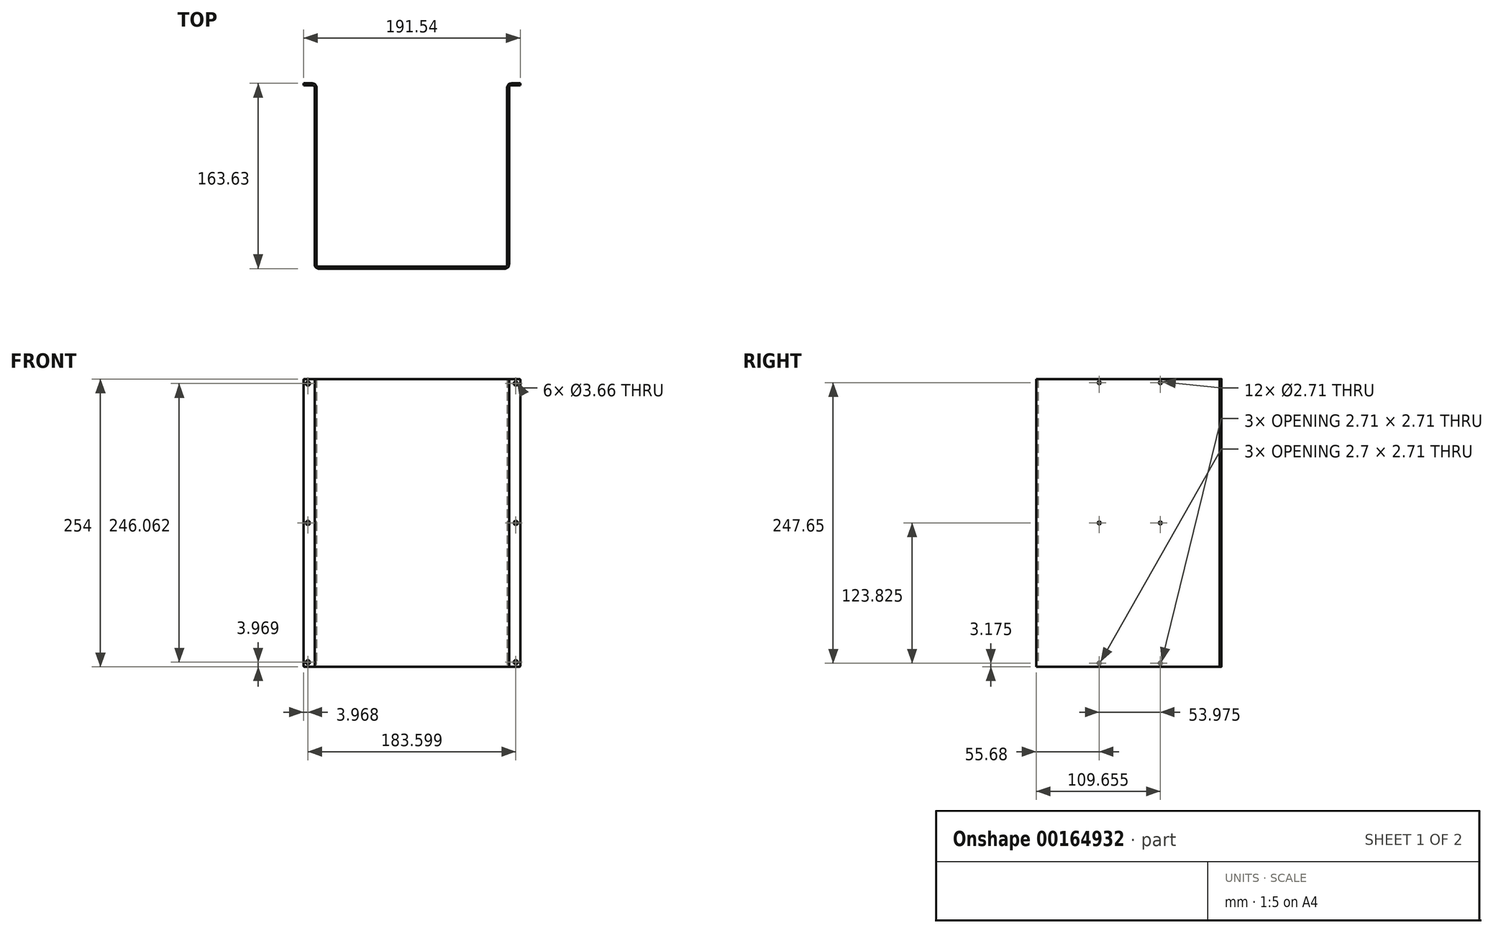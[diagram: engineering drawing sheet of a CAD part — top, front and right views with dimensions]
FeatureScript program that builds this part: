
annotation { "Feature Type Name" : "Feature", "Feature Type Description" : "" }
export const myFeature = defineFeature(function(context is Context, id is Id, definition is map)
    precondition{}
    {
        {
            var Q0;
            Q0=qCreatedBy(makeId("Top.planeOp"),FACE);
            var sketch = newSketch(context, id + "F0", { "sketchPlane" : qUnion([Q0])});
            skLineSegment(sketch, "E0", {"start": v(0, 0) * mm, "end": v(0, -161.93) * mm});
            skLineSegment(sketch, "E1", {"start": v(-1.7, -163.63) * mm, "end": v(-1.7, -1.7) * mm});
            skLineSegment(sketch, "E2", {"start": v(168.28, -161.93) * mm, "end": v(168.28, 0) * mm});
            skLineSegment(sketch, "E3", {"start": v(169.98, -1.7) * mm, "end": v(169.98, -163.63) * mm});
            skLineSegment(sketch, "E4", {"start": v(-1.7, -163.63) * mm, "end": v(169.98, -163.63) * mm});
            skLineSegment(sketch, "E5", {"start": v(0, -161.93) * mm, "end": v(168.28, -161.93) * mm});
            skLineSegment(sketch, "E6", {"start": v(168.27, 0) * mm, "end": v(179.9, 0) * mm});
            skLineSegment(sketch, "E7", {"start": v(179.9, 0) * mm, "end": v(179.9, -1.7) * mm});
            skLineSegment(sketch, "E8", {"start": v(179.9, -1.7) * mm, "end": v(169.98, -1.7) * mm});
            skLineSegment(sketch, "E9", {"start": v(0, 0) * mm, "end": v(-11.63, 0) * mm});
            skLineSegment(sketch, "E10", {"start": v(-11.63, 0) * mm, "end": v(-11.63, -1.7) * mm});
            skLineSegment(sketch, "E11", {"start": v(-11.63, -1.7) * mm, "end": v(-1.7, -1.7) * mm});
            skLineSegment(sketch, "E12", {"start": v(84.14, -161.93) * mm, "end": v(84.14, -163.63) * mm, "construction": true});
            skLineSegment(sketch, "E13", {"start": v(-1.7, -1.7) * mm, "end": v(0, -1.7) * mm, "construction": true});
            skLineSegment(sketch, "E14", {"start": v(169.98, -1.7) * mm, "end": v(168.27, -1.7) * mm, "construction": true});
            skSolve(sketch);
        }
        {
            var Q0;
            Q0=qSketchRegion(id+"F0",true);
            extrude(context, id + "F1", {"entities" : qUnion([Q0]), "depth" : 254 * mm});
        }
        {
            var Q0;
            Q0=makeQuery(id+"F1.opExtrude","SWEPT_EDGE",EDGE,{"disambiguationData":[OSD([sQuery(id+"F0.wireOp",EDGE,"E2"),sQuery(id+"F0.wireOp",EDGE,"E5")])]});
            var Q1;
            Q1=makeQuery(id+"F1.opExtrude","SWEPT_EDGE",EDGE,{"disambiguationData":[OSD([sQuery(id+"F0.wireOp",EDGE,"E0"),sQuery(id+"F0.wireOp",EDGE,"E5")])]});
            var Q2;
            Q2=makeQuery(id+"F1.opExtrude","SWEPT_EDGE",EDGE,{"disambiguationData":[OSD([sQuery(id+"F0.wireOp",EDGE,"E0"),sQuery(id+"F0.wireOp",EDGE,"E5")])]});
            var Q3;
            Q3=makeQuery(id+"F1.opExtrude","SWEPT_EDGE",EDGE,{"disambiguationData":[OSD([sQuery(id+"F0.wireOp",EDGE,"E2"),sQuery(id+"F0.wireOp",EDGE,"E5")])]});
            var Q4;
            Q4=makeQuery(id+"F1.opExtrude","SWEPT_EDGE",EDGE,{"disambiguationData":[OSD([sQuery(id+"F0.wireOp",EDGE,"E1"),sQuery(id+"F0.wireOp",EDGE,"E11")])]});
            var Q5;
            Q5=makeQuery(id+"F1.opExtrude","SWEPT_EDGE",EDGE,{"disambiguationData":[OSD([sQuery(id+"F0.wireOp",EDGE,"E3"),sQuery(id+"F0.wireOp",EDGE,"E8")])]});
            fillet(context, id + "F2", {"entities" : qUnion([Q0, Q1, Q2, Q3, Q4, Q5]), "radius" : 1.98 * mm, "tangentPropagation" : true, "allowEdgeOverflow" : false});
        }
        {
            var Q0;
            Q0=makeQuery(id+"F1.opExtrude","SWEPT_EDGE",EDGE,{"disambiguationData":[OSD([sQuery(id+"F0.wireOp",EDGE,"E0"),sQuery(id+"F0.wireOp",EDGE,"E9")])]});
            var Q1;
            Q1=makeQuery(id+"F1.opExtrude","SWEPT_EDGE",EDGE,{"disambiguationData":[OSD([sQuery(id+"F0.wireOp",EDGE,"E1"),sQuery(id+"F0.wireOp",EDGE,"E4")])]});
            var Q2;
            Q2=makeQuery(id+"F1.opExtrude","SWEPT_EDGE",EDGE,{"disambiguationData":[OSD([sQuery(id+"F0.wireOp",EDGE,"E3"),sQuery(id+"F0.wireOp",EDGE,"E4")])]});
            var Q3;
            Q3=makeQuery(id+"F1.opExtrude","SWEPT_EDGE",EDGE,{"disambiguationData":[OSD([sQuery(id+"F0.wireOp",EDGE,"E2"),sQuery(id+"F0.wireOp",EDGE,"E6")])]});
            fillet(context, id + "F3", {"entities" : qUnion([Q0, Q1, Q2, Q3]), "radius" : 3.7 * mm, "tangentPropagation" : true, "allowEdgeOverflow" : false});
        }
        {
            var Q0;
            Q0=makeQuery(id+"F1.opExtrude","SWEPT_FACE",FACE,{"disambiguationData":[OSD([sQuery(id+"F0.wireOp",EDGE,"E1")])]});
            var sketch = newSketch(context, id + "F4", { "sketchPlane" : qUnion([Q0])});
            skLineSegment(sketch, "E15", {"start": v(3.7, 127) * mm, "end": v(80.96, 127) * mm, "construction": true});
            skLineSegment(sketch, "E16.bottom", {"start": v(53.98, 3.18) * mm, "end": v(107.95, 3.18) * mm, "construction": true});
            skLineSegment(sketch, "E16.top", {"start": v(53.98, 250.83) * mm, "end": v(107.95, 250.83) * mm, "construction": true});
            skLineSegment(sketch, "E16.left", {"start": v(53.98, 3.17) * mm, "end": v(53.98, 250.83) * mm, "construction": true});
            skLineSegment(sketch, "E16.right", {"start": v(107.95, 3.17) * mm, "end": v(107.95, 250.83) * mm, "construction": true});
            skPoint(sketch, "E16.middle", {"position": v(80.96, 127) * mm});
            skLineSegment(sketch, "E17", {"start": v(80.96, 3.18) * mm, "end": v(80.96, 0) * mm, "construction": true});
            skCircle(sketch, "E18", {"center": v(107.95, 3.17) * mm, "radius": 1.35 * mm});
            skCircle(sketch, "E19", {"center": v(53.98, 3.17) * mm, "radius": 1.35 * mm});
            skCircle(sketch, "E20", {"center": v(53.98, 250.83) * mm, "radius": 1.35 * mm});
            skCircle(sketch, "E21", {"center": v(107.95, 250.83) * mm, "radius": 1.35 * mm});
            skCircle(sketch, "E22", {"center": v(107.95, 127) * mm, "radius": 1.35 * mm});
            skCircle(sketch, "E23", {"center": v(53.98, 127) * mm, "radius": 1.35 * mm});
            skSolve(sketch);
        }
        {
            var Q0;
            Q0 = qSketchRegion(id + "F4", true);
            var Q1;
            Q1=makeQuery(id+"F1.opExtrude","SWEPT_FACE",FACE,{"disambiguationData":[OSD([sQuery(id+"F0.wireOp",EDGE,"E3")])]});
            extrude(context, id + "F5", {"entities" : qUnion([Q0]), "operationType" : NewBodyOperationType.REMOVE, "endBound" : BoundingType.UP_TO_SURFACE, "oppositeDirection" : true, "endBoundEntityFace" : qUnion([Q1]), "depth" : 25.4 * mm});
        }
        {
            var Q0;
            Q0=makeQuery(id+"F1.opExtrude","SWEPT_FACE",FACE,{"disambiguationData":[OSD([sQuery(id+"F0.wireOp",EDGE,"E9")])]});
            var sketch = newSketch(context, id + "F6", { "sketchPlane" : qUnion([Q0])});
            skLineSegment(sketch, "E24", {"start": v(-171.97, 127) * mm, "end": v(3.7, 127) * mm, "construction": true});
            skLineSegment(sketch, "E25.bottom", {"start": v(-175.94, 254) * mm, "end": v(-179.9, 254) * mm, "construction": true});
            skLineSegment(sketch, "E25.top", {"start": v(-175.94, 250.03) * mm, "end": v(-179.9, 250.03) * mm, "construction": true});
            skLineSegment(sketch, "E25.left", {"start": v(-175.94, 254) * mm, "end": v(-175.94, 250.03) * mm, "construction": true});
            skLineSegment(sketch, "E25.right", {"start": v(-179.9, 254) * mm, "end": v(-179.9, 250.03) * mm, "construction": true});
            skLineSegment(sketch, "E26.bottom", {"start": v(-175.94, 250.03) * mm, "end": v(7.66, 250.03) * mm, "construction": true});
            skLineSegment(sketch, "E26.top", {"start": v(-175.94, 3.97) * mm, "end": v(7.66, 3.97) * mm, "construction": true});
            skLineSegment(sketch, "E26.left", {"start": v(-175.94, 250.03) * mm, "end": v(-175.94, 3.97) * mm, "construction": true});
            skLineSegment(sketch, "E26.right", {"start": v(7.66, 250.03) * mm, "end": v(7.66, 3.97) * mm, "construction": true});
            skPoint(sketch, "E26.middle", {"position": v(-84.14, 127) * mm});
            skCircle(sketch, "E27", {"center": v(-175.94, 250.03) * mm, "radius": 1.83 * mm});
            skCircle(sketch, "E28", {"center": v(-175.94, 127) * mm, "radius": 1.83 * mm});
            skCircle(sketch, "E29", {"center": v(-175.94, 3.97) * mm, "radius": 1.83 * mm});
            skCircle(sketch, "E30", {"center": v(7.66, 3.97) * mm, "radius": 1.83 * mm});
            skCircle(sketch, "E31", {"center": v(7.66, 127) * mm, "radius": 1.83 * mm});
            skCircle(sketch, "E32", {"center": v(7.66, 250.03) * mm, "radius": 1.83 * mm});
            skSolve(sketch);
        }
        {
            var Q0;
            Q0 = qSketchRegion(id + "F6", true);
            var Q1;
            Q1=makeQuery(id+"F1.opExtrude","SWEPT_FACE",FACE,{"disambiguationData":[OSD([sQuery(id+"F0.wireOp",EDGE,"E8")])]});
            extrude(context, id + "F7", {"entities" : qUnion([Q0]), "operationType" : NewBodyOperationType.REMOVE, "endBound" : BoundingType.UP_TO_SURFACE, "oppositeDirection" : true, "endBoundEntityFace" : qUnion([Q1]), "depth" : 25.4 * mm});
        }
        {
            var Q0;
            Q0=makeQuery(id+"F1.opExtrude","CAP_EDGE",EDGE,{"disambiguationData":[OSD([sQuery(id+"F0.wireOp",EDGE,"E10")])],"isStart":true});
            var Q1;
            Q1=makeQuery(id+"F1.opExtrude","CAP_EDGE",EDGE,{"disambiguationData":[OSD([sQuery(id+"F0.wireOp",EDGE,"E10")])],"isStart":false});
            var Q2;
            Q2=makeQuery(id+"F1.opExtrude","CAP_EDGE",EDGE,{"disambiguationData":[OSD([sQuery(id+"F0.wireOp",EDGE,"E7")])],"isStart":false});
            var Q3;
            Q3=makeQuery(id+"F1.opExtrude","CAP_EDGE",EDGE,{"disambiguationData":[OSD([sQuery(id+"F0.wireOp",EDGE,"E7")])],"isStart":true});
            fillet(context, id + "F8", {"entities" : qUnion([Q0, Q1, Q2, Q3]), "radius" : 0.76 * mm, "tangentPropagation" : true, "allowEdgeOverflow" : false});
        }
    });
